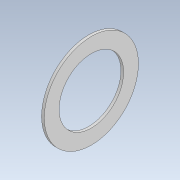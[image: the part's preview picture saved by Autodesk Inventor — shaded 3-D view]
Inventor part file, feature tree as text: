
AUTODESK INVENTOR PART (.ipt)
format: ipt  version: 2021 (Build 250183000, 183)  size: 85,504 bytes
history: native  units: mm
features: other x1, extrude x1, sketch x1
ambient origin geometry x8: Origin, YZ Plane, XZ Plane, XY Plane, X Axis, Y Axis, Z Axis, Center Point
bodies: Body1 (feature_tree)
feature tree (3):
  other  "Sólido1"
  extrude  "Extrusión1"  [1 undecoded]
  sketch  "Boceto1"  dims[d2=1.0mm d3=0.0mm]
note: 1 required parameter value undecoded (feature->parameter linkage not recoverable at this tier; creation-order binding heuristic only, values carry confidence <= 0.55)
